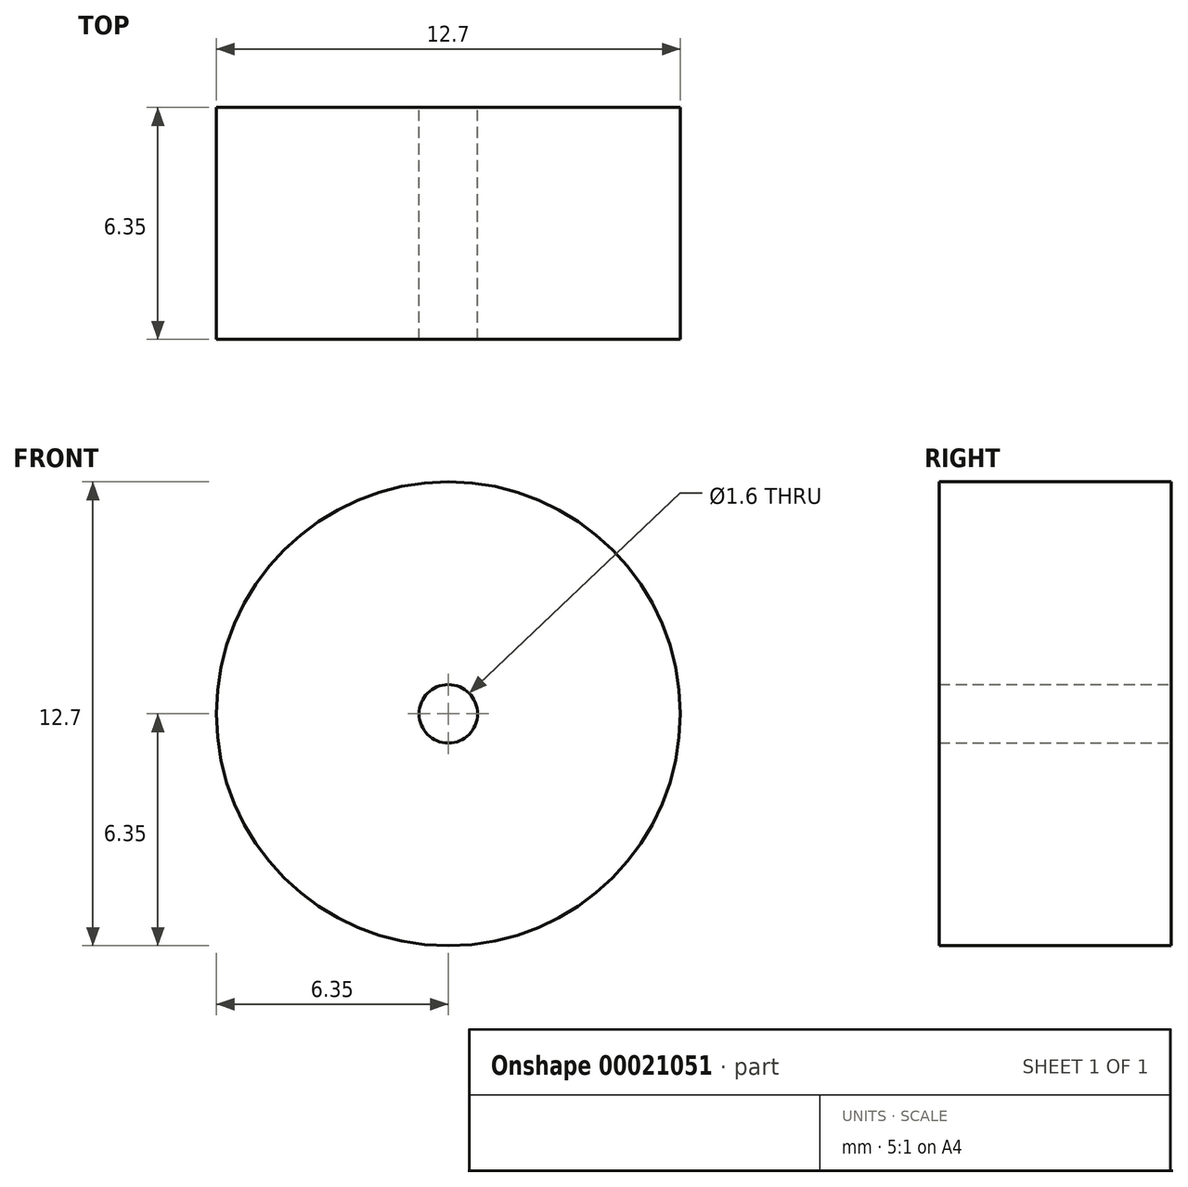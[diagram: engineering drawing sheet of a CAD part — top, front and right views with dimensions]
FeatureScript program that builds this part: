
annotation { "Feature Type Name" : "Feature", "Feature Type Description" : "" }
export const myFeature = defineFeature(function(context is Context, id is Id, definition is map)
    precondition{}
    {
        {
            var Q0;
            Q0=qCreatedBy(makeId("Front.planeOp"),FACE);
            var sketch = newSketch(context, id + "F0", { "sketchPlane" : qUnion([Q0])});
            skCircle(sketch, "E0", {"center": v(0, 0) * mm, "radius": 6.35 * mm});
            skCircle(sketch, "E1", {"center": v(0, 0) * mm, "radius": 0.8 * mm});
            skSolve(sketch);
        }
        {
            var Q0;
            Q0 = qSketchRegion(id + "F0", true);
            extrude(context, id + "F1", {"entities" : qUnion([Q0]), "depth" : 6.35 * mm});
        }
    });
